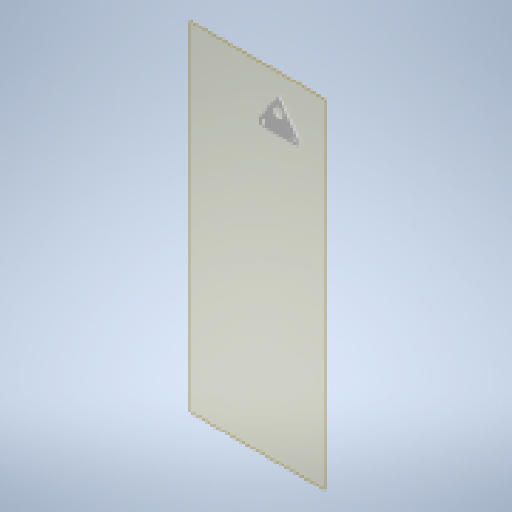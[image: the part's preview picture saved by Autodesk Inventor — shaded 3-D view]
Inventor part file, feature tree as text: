
AUTODESK INVENTOR PART (.ipt)
format: ipt  version: 2024.2 (Build 282272000, 272)  size: 130,560 bytes
history: native  units: mm
features: other x5, reference x2, extrude x1, sketch x1
ambient origin geometry x8: Origin, YZ Plane, XZ Plane, XY Plane, X Axis, Y Axis, Z Axis, Center Point
bodies: Body1 (feature_tree)
feature tree (9):
  other  "Твердое тело1"
  other  "РабПлоскость1"
  extrude  "Выдавливание1"  Depth=2.0mm TaperAngle=0.0deg
  sketch  "Эскиз1"
  reference  "Ссылка1"
  reference  "Ссылка2"
  other  "<userpath>\Documents\Artist-v2\3D\Робот.iam"
  other  "Робот.iam"
  other  "бок:1"
